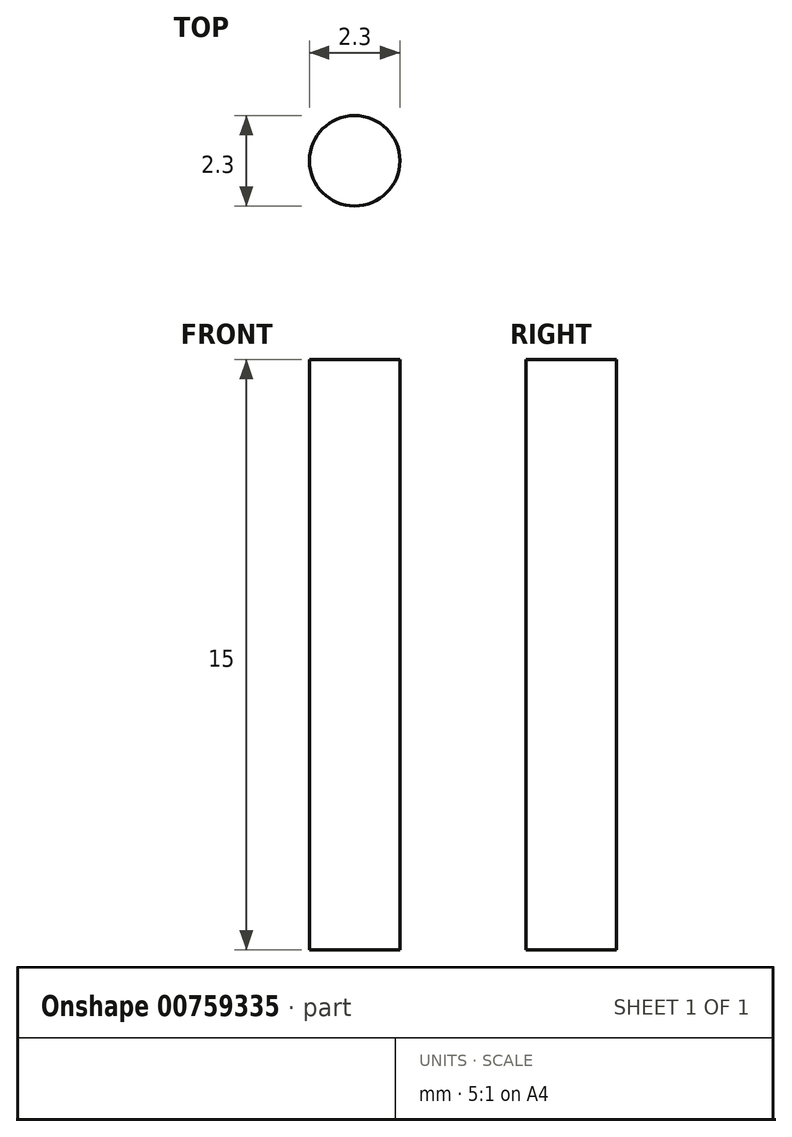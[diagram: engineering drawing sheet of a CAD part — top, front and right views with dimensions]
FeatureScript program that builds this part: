
annotation { "Feature Type Name" : "Feature", "Feature Type Description" : "" }
export const myFeature = defineFeature(function(context is Context, id is Id, definition is map)
    precondition{}
    {
        {
            var Q0;
            Q0=qCreatedBy(makeId("Top.planeOp"),FACE);
            var sketch = newSketch(context, id + "F0", { "sketchPlane" : qUnion([Q0])});
            skCircle(sketch, "E0", {"center": v(0, 0) * mm, "radius": 1.15 * mm});
            skSolve(sketch);
        }
        {
            var Q0;
            Q0 = qSketchRegion(id + "F0", true);
            extrude(context, id + "F1", {"entities" : qUnion([Q0]), "depth" : 15 * mm, "offsetDistance" : 25 * mm});
        }
    });
